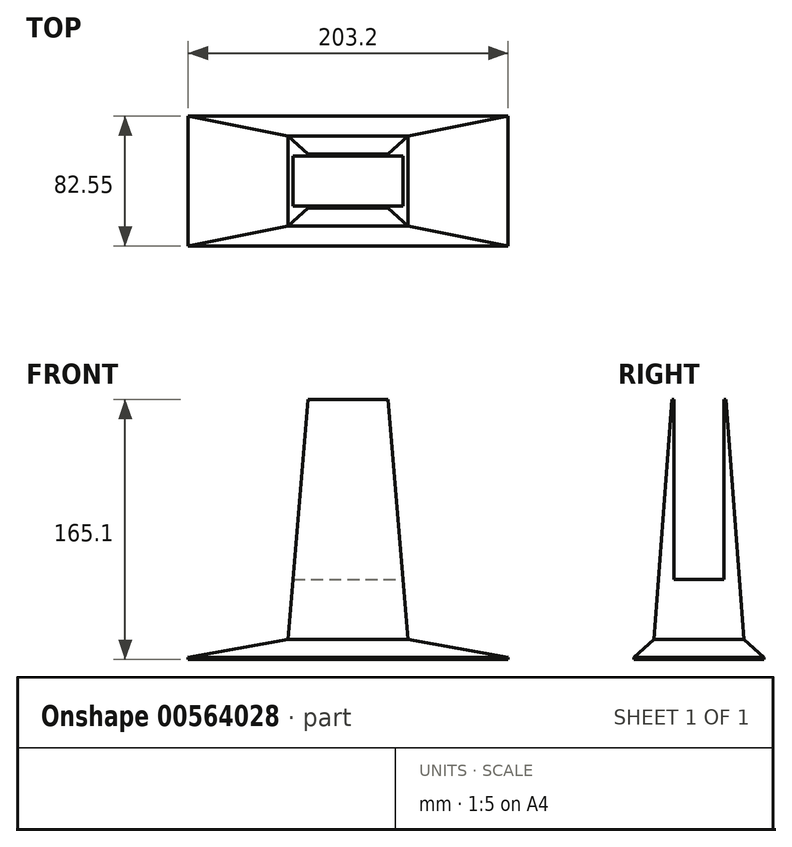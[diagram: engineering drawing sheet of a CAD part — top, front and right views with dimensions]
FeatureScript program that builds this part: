
annotation { "Feature Type Name" : "Feature", "Feature Type Description" : "" }
export const myFeature = defineFeature(function(context is Context, id is Id, definition is map)
    precondition{}
    {
        {
            var Q0;
            Q0=qCreatedBy(makeId("Top.planeOp"),FACE);
            var sketch = newSketch(context, id + "F0", { "sketchPlane" : qUnion([Q0])});
            skLineSegment(sketch, "E0.bottom", {"start": v(0, 0) * mm, "end": v(203.2, 0) * mm});
            skLineSegment(sketch, "E0.top", {"start": v(0, 82.55) * mm, "end": v(203.2, 82.55) * mm});
            skLineSegment(sketch, "E0.left", {"start": v(0, 0) * mm, "end": v(0, 82.55) * mm});
            skLineSegment(sketch, "E0.right", {"start": v(203.2, 0) * mm, "end": v(203.2, 82.55) * mm});
            skSolve(sketch);
        }
        {
            var Q0;
            Q0 = qSketchRegion(id + "F0", true);
            extrude(context, id + "F1", {"entities" : qUnion([Q0]), "depth" : 12.7 * mm, "offsetDistance" : 25.4 * mm});
        }
        {
            var Q0;
            Q0=makeQuery(id+"F1.opExtrude","SWEPT_FACE",FACE,{"disambiguationData":[OSD([sQuery(id+"F0.wireOp",EDGE,"E0.right")])]});
            var sketch = newSketch(context, id + "F2", { "sketchPlane" : qUnion([Q0])});
            skLineSegment(sketch, "E1", {"start": v(0, 12.7) * mm, "end": v(12.7, 12.7) * mm});
            skLineSegment(sketch, "E2", {"start": v(12.7, 12.7) * mm, "end": v(0, 1.27) * mm});
            skLineSegment(sketch, "E3", {"start": v(0, 1.27) * mm, "end": v(0, 12.7) * mm});
            skLineSegment(sketch, "E4", {"start": v(82.55, 12.7) * mm, "end": v(69.85, 12.7) * mm});
            skLineSegment(sketch, "E5", {"start": v(69.85, 12.7) * mm, "end": v(82.55, 1.27) * mm});
            skLineSegment(sketch, "E6", {"start": v(82.55, 1.27) * mm, "end": v(82.55, 12.7) * mm});
            skSolve(sketch);
        }
        {
            var Q0;
            Q0 = qSketchRegion(id + "F2", true);
            extrude(context, id + "F3", {"entities" : qUnion([Q0]), "operationType" : NewBodyOperationType.REMOVE, "oppositeDirection" : true, "depth" : 203.2 * mm, "offsetDistance" : 25.4 * mm});
        }
        {
            var Q0;
            Q0=makeQuery(id+"F1.opExtrude","SWEPT_FACE",FACE,{"disambiguationData":[OSD([sQuery(id+"F0.wireOp",EDGE,"E0.top")])]});
            var sketch = newSketch(context, id + "F4", { "sketchPlane" : qUnion([Q0])});
            skLineSegment(sketch, "E7", {"start": v(-203.2, 1.27) * mm, "end": v(-203.2, 12.7) * mm});
            skLineSegment(sketch, "E8", {"start": v(-203.2, 12.7) * mm, "end": v(-139.7, 12.7) * mm});
            skLineSegment(sketch, "E9", {"start": v(-139.7, 12.7) * mm, "end": v(-203.2, 1.27) * mm});
            skLineSegment(sketch, "E10", {"start": v(0, 1.27) * mm, "end": v(0, 12.7) * mm});
            skLineSegment(sketch, "E11", {"start": v(0, 12.7) * mm, "end": v(-63.5, 12.7) * mm});
            skLineSegment(sketch, "E12", {"start": v(-63.5, 12.7) * mm, "end": v(0, 1.27) * mm});
            skSolve(sketch);
        }
        {
            var Q0;
            Q0 = qSketchRegion(id + "F4", true);
            extrude(context, id + "F5", {"entities" : qUnion([Q0]), "operationType" : NewBodyOperationType.REMOVE, "oppositeDirection" : true, "depth" : 82.55 * mm, "offsetDistance" : 25.4 * mm});
        }
        {
            var Q0;
            Q0=makeQuery(id+"F1.opExtrude","CAP_FACE",FACE,{"disambiguationData":[OSD([sQuery(id+"F0.wireOp",EDGE,"E0.bottom"),sQuery(id+"F0.wireOp",EDGE,"E0.top"),sQuery(id+"F0.wireOp",EDGE,"E0.left"),sQuery(id+"F0.wireOp",EDGE,"E0.right")])],"isStart":false});
            var sketch = newSketch(context, id + "F6", { "sketchPlane" : qUnion([Q0])});
            skLineSegment(sketch, "E13.bottom", {"start": v(63.5, 69.85) * mm, "end": v(139.7, 69.85) * mm});
            skLineSegment(sketch, "E13.top", {"start": v(63.5, 12.7) * mm, "end": v(139.7, 12.7) * mm});
            skLineSegment(sketch, "E13.left", {"start": v(63.5, 69.85) * mm, "end": v(63.5, 12.7) * mm});
            skLineSegment(sketch, "E13.right", {"start": v(139.7, 69.85) * mm, "end": v(139.7, 12.7) * mm});
            skSolve(sketch);
        }
        {
            var Q0;
            Q0 = qSketchRegion(id + "F6", true);
            extrude(context, id + "F7", {"entities" : qUnion([Q0]), "depth" : 152.4 * mm, "offsetDistance" : 25.4 * mm});
        }
        {
            var Q0;
            Q0=makeQuery(id+"F7.opExtrude","SWEPT_FACE",FACE,{"disambiguationData":[OSD([sQuery(id+"F6.wireOp",EDGE,"E13.right")])]});
            var sketch = newSketch(context, id + "F8", { "sketchPlane" : qUnion([Q0])});
            skLineSegment(sketch, "E14.bottom", {"start": v(25.4, 165.1) * mm, "end": v(57.15, 165.1) * mm});
            skLineSegment(sketch, "E14.top", {"start": v(25.4, 50.8) * mm, "end": v(57.15, 50.8) * mm});
            skLineSegment(sketch, "E14.left", {"start": v(25.4, 165.1) * mm, "end": v(25.4, 50.8) * mm});
            skLineSegment(sketch, "E14.right", {"start": v(57.15, 165.1) * mm, "end": v(57.15, 50.8) * mm});
            skSolve(sketch);
        }
        {
            var Q0;
            Q0=makeQuery(id+"F8.imprint","IMPRINT",FACE,{"disambiguationData":[TD([[makeQuery(id+"F8.imprint","IMPRINT",EDGE,{"derivedFrom":sQuery(id+"F8.wireOp",EDGE,"E14.bottom")}),-1.0]])]});
            extrude(context, id + "F9", {"entities" : qUnion([Q0]), "operationType" : NewBodyOperationType.REMOVE, "oppositeDirection" : true, "depth" : 76.2 * mm, "offsetDistance" : 25.4 * mm});
        }
        {
            var Q0;
            Q0=makeQuery(id+"F7.opExtrude","SWEPT_FACE",FACE,{"disambiguationData":[OSD([sQuery(id+"F6.wireOp",EDGE,"E13.right")])]});
            var sketch = newSketch(context, id + "F10", { "sketchPlane" : qUnion([Q0])});
            skLineSegment(sketch, "E15", {"start": v(12.7, 12.7) * mm, "end": v(12.7, 165.1) * mm});
            skLineSegment(sketch, "E16", {"start": v(12.7, 165.1) * mm, "end": v(24.13, 165.1) * mm});
            skLineSegment(sketch, "E17", {"start": v(24.13, 165.1) * mm, "end": v(12.7, 12.7) * mm});
            skLineSegment(sketch, "E18", {"start": v(69.85, 12.7) * mm, "end": v(69.85, 165.1) * mm});
            skLineSegment(sketch, "E19", {"start": v(69.85, 165.1) * mm, "end": v(58.42, 165.1) * mm});
            skLineSegment(sketch, "E20", {"start": v(58.42, 165.1) * mm, "end": v(69.85, 12.7) * mm});
            skSolve(sketch);
        }
        {
            var Q0;
            Q0=makeQuery(id+"F7.opExtrude","SWEPT_FACE",FACE,{"disambiguationData":[OSD([sQuery(id+"F6.wireOp",EDGE,"E13.top")])]});
            var sketch = newSketch(context, id + "F11", { "sketchPlane" : qUnion([Q0])});
            skLineSegment(sketch, "E21", {"start": v(63.5, 165.1) * mm, "end": v(63.5, 12.7) * mm});
            skLineSegment(sketch, "E22", {"start": v(63.5, 12.7) * mm, "end": v(76.2, 165.1) * mm});
            skLineSegment(sketch, "E23", {"start": v(76.2, 165.1) * mm, "end": v(63.5, 165.1) * mm});
            skLineSegment(sketch, "E24", {"start": v(139.7, 165.1) * mm, "end": v(127, 165.1) * mm});
            skLineSegment(sketch, "E25", {"start": v(127, 165.1) * mm, "end": v(139.7, 12.7) * mm});
            skLineSegment(sketch, "E26", {"start": v(139.7, 12.7) * mm, "end": v(139.7, 165.1) * mm});
            skSolve(sketch);
        }
        {
            var Q0;
            Q0 = qSketchRegion(id + "F10", true);
            extrude(context, id + "F12", {"entities" : qUnion([Q0]), "operationType" : NewBodyOperationType.REMOVE, "oppositeDirection" : true, "depth" : 76.2 * mm, "offsetDistance" : 25.4 * mm});
        }
        {
            var Q0;
            Q0 = qSketchRegion(id + "F11", true);
            extrude(context, id + "F13", {"entities" : qUnion([Q0]), "operationType" : NewBodyOperationType.REMOVE, "oppositeDirection" : true, "depth" : 57.15 * mm, "offsetDistance" : 25.4 * mm});
        }
    });
